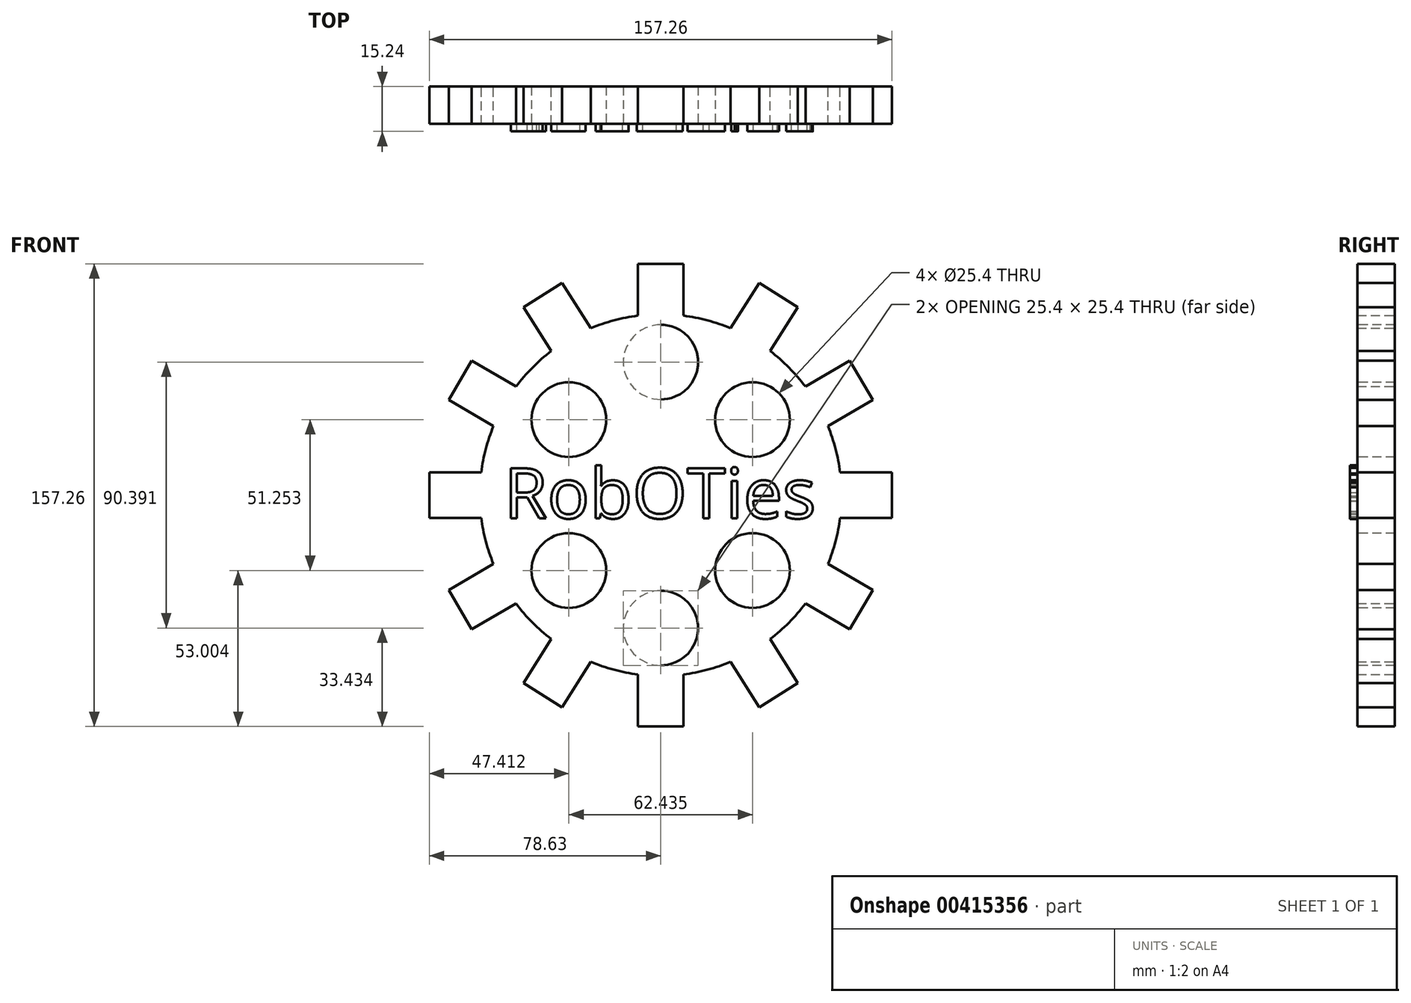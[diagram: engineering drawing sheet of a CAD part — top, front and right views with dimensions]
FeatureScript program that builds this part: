
annotation { "Feature Type Name" : "Feature", "Feature Type Description" : "" }
export const myFeature = defineFeature(function(context is Context, id is Id, definition is map)
    precondition{}
    {
        {
            var Q0;
            Q0=qCreatedBy(makeId("Front.planeOp"),FACE);
            var sketch = newSketch(context, id + "F0", { "sketchPlane" : qUnion([Q0])});
            skArc(sketch, "E0", {"start": v(-61, 7.73) * mm, "mid": v(-59.45, 15.72) * mm, "end": v(-56.85, 23.43) * mm});
            skLineSegment(sketch, "E1", {"start": v(-61, 7.73) * mm, "end": v(-78.63, 7.73) * mm});
            skLineSegment(sketch, "E2", {"start": v(-78.63, 7.73) * mm, "end": v(-78.63, 0) * mm});
            skPoint(sketch, "E3.orphan", {"position": v(-61.49, 0) * mm});
            skLineSegment(sketch, "E4", {"start": v(-56.85, 23.43) * mm, "end": v(-72.07, 32.3) * mm});
            skLineSegment(sketch, "E5", {"start": v(-72.07, 32.3) * mm, "end": v(-64.28, 45.66) * mm});
            skLineSegment(sketch, "E6", {"start": v(-64.28, 45.66) * mm, "end": v(-49.2, 36.87) * mm});
            skArc(sketch, "E7.trimOffspring", {"start": v(-49.2, 36.87) * mm, "mid": v(-43.62, 43.33) * mm, "end": v(-37.2, 48.96) * mm});
            skLineSegment(sketch, "E8", {"start": v(-37.2, 48.96) * mm, "end": v(-46.61, 63.86) * mm});
            skLineSegment(sketch, "E9", {"start": v(-46.61, 63.86) * mm, "end": v(-33.54, 72.13) * mm});
            skLineSegment(sketch, "E10", {"start": v(-33.54, 72.13) * mm, "end": v(-23.78, 56.7) * mm});
            skArc(sketch, "E11.trimOffspring", {"start": v(-23.78, 56.7) * mm, "mid": v(-15.91, 59.4) * mm, "end": v(-7.75, 61) * mm});
            skLineSegment(sketch, "E12", {"start": v(-7.75, 61) * mm, "end": v(-7.75, 78.63) * mm});
            skLineSegment(sketch, "E13", {"start": v(-7.75, 78.63) * mm, "end": v(0, 78.63) * mm});
            skPoint(sketch, "E14.orphan", {"position": v(0, 61.49) * mm});
            skLineSegment(sketch, "E15", {"start": v(0, -76.88) * mm, "end": v(0, 112.3) * mm, "construction": true});
            skLineSegment(sketch, "E16", {"start": v(103.9, 0) * mm, "end": v(-126.27, 0) * mm, "construction": true});
            skLineSegment(sketch, "E17.MirrorCS", {"start": v(7.75, 61) * mm, "end": v(7.75, 78.63) * mm});
            skLineSegment(sketch, "E18.MirrorCS", {"start": v(7.75, 78.63) * mm, "end": v(0, 78.63) * mm});
            skArc(sketch, "E19.MirrorCS", {"start": v(23.78, 56.7) * mm, "mid": v(15.91, 59.4) * mm, "end": v(7.75, 61) * mm});
            skLineSegment(sketch, "E20.MirrorCS", {"start": v(33.54, 72.13) * mm, "end": v(23.78, 56.7) * mm});
            skLineSegment(sketch, "E21.MirrorCS", {"start": v(46.61, 63.86) * mm, "end": v(33.54, 72.13) * mm});
            skLineSegment(sketch, "E22.MirrorCS", {"start": v(37.2, 48.96) * mm, "end": v(46.61, 63.86) * mm});
            skArc(sketch, "E23.MirrorCS", {"start": v(49.2, 36.87) * mm, "mid": v(43.62, 43.33) * mm, "end": v(37.2, 48.96) * mm});
            skLineSegment(sketch, "E24.MirrorCS", {"start": v(64.28, 45.66) * mm, "end": v(49.2, 36.87) * mm});
            skLineSegment(sketch, "E25.MirrorCS", {"start": v(72.07, 32.3) * mm, "end": v(64.28, 45.66) * mm});
            skLineSegment(sketch, "E26.MirrorCS", {"start": v(56.85, 23.43) * mm, "end": v(72.07, 32.3) * mm});
            skArc(sketch, "E27.MirrorCS", {"start": v(61, 7.73) * mm, "mid": v(59.45, 15.72) * mm, "end": v(56.85, 23.43) * mm});
            skLineSegment(sketch, "E28.MirrorCS", {"start": v(61, 7.73) * mm, "end": v(78.63, 7.73) * mm});
            skLineSegment(sketch, "E29.MirrorCS", {"start": v(78.63, 7.73) * mm, "end": v(78.63, 0) * mm});
            skLineSegment(sketch, "E30.MirrorCS", {"start": v(-78.63, -7.73) * mm, "end": v(-78.63, 0) * mm});
            skLineSegment(sketch, "E31.MirrorCS", {"start": v(-61, -7.73) * mm, "end": v(-78.63, -7.73) * mm});
            skArc(sketch, "E32.MirrorCS", {"start": v(-61, -7.73) * mm, "mid": v(-59.45, -15.72) * mm, "end": v(-56.85, -23.43) * mm});
            skLineSegment(sketch, "E33.MirrorCS", {"start": v(-56.85, -23.43) * mm, "end": v(-72.07, -32.3) * mm});
            skLineSegment(sketch, "E34.MirrorCS", {"start": v(-72.07, -32.3) * mm, "end": v(-64.28, -45.66) * mm});
            skLineSegment(sketch, "E35.MirrorCS", {"start": v(-64.28, -45.66) * mm, "end": v(-49.2, -36.87) * mm});
            skArc(sketch, "E36.MirrorCS", {"start": v(-49.2, -36.87) * mm, "mid": v(-43.62, -43.33) * mm, "end": v(-37.2, -48.96) * mm});
            skLineSegment(sketch, "E37.MirrorCS", {"start": v(-37.2, -48.96) * mm, "end": v(-46.61, -63.86) * mm});
            skLineSegment(sketch, "E38.MirrorCS", {"start": v(-46.61, -63.86) * mm, "end": v(-33.54, -72.13) * mm});
            skLineSegment(sketch, "E39.MirrorCS", {"start": v(-33.54, -72.13) * mm, "end": v(-23.78, -56.7) * mm});
            skArc(sketch, "E40.MirrorCS", {"start": v(-23.78, -56.7) * mm, "mid": v(-15.91, -59.4) * mm, "end": v(-7.75, -61) * mm});
            skLineSegment(sketch, "E41.MirrorCS", {"start": v(-7.75, -61) * mm, "end": v(-7.75, -78.63) * mm});
            skLineSegment(sketch, "E42.MirrorCS", {"start": v(-7.75, -78.63) * mm, "end": v(0, -78.63) * mm});
            skLineSegment(sketch, "E43.MirrorCS", {"start": v(7.75, -78.63) * mm, "end": v(0, -78.63) * mm});
            skLineSegment(sketch, "E44.MirrorCS", {"start": v(7.75, -61) * mm, "end": v(7.75, -78.63) * mm});
            skArc(sketch, "E45.MirrorCS", {"start": v(23.78, -56.7) * mm, "mid": v(15.91, -59.4) * mm, "end": v(7.75, -61) * mm});
            skLineSegment(sketch, "E46.MirrorCS", {"start": v(33.54, -72.13) * mm, "end": v(23.78, -56.7) * mm});
            skLineSegment(sketch, "E47.MirrorCS", {"start": v(46.61, -63.86) * mm, "end": v(33.54, -72.13) * mm});
            skLineSegment(sketch, "E48.MirrorCS", {"start": v(37.2, -48.96) * mm, "end": v(46.61, -63.86) * mm});
            skArc(sketch, "E49.MirrorCS", {"start": v(49.2, -36.87) * mm, "mid": v(43.62, -43.33) * mm, "end": v(37.2, -48.96) * mm});
            skLineSegment(sketch, "E50.MirrorCS", {"start": v(64.28, -45.66) * mm, "end": v(49.2, -36.87) * mm});
            skLineSegment(sketch, "E51.MirrorCS", {"start": v(72.07, -32.3) * mm, "end": v(64.28, -45.66) * mm});
            skLineSegment(sketch, "E52.MirrorCS", {"start": v(56.85, -23.43) * mm, "end": v(72.07, -32.3) * mm});
            skArc(sketch, "E53.MirrorCS", {"start": v(61, -7.73) * mm, "mid": v(59.45, -15.72) * mm, "end": v(56.85, -23.43) * mm});
            skLineSegment(sketch, "E54.MirrorCS", {"start": v(61, -7.73) * mm, "end": v(78.63, -7.73) * mm});
            skLineSegment(sketch, "E55.MirrorCS", {"start": v(78.63, -7.73) * mm, "end": v(78.63, 0) * mm});
            skSolve(sketch);
        }
        {
            var Q0;
            Q0 = qSketchRegion(id + "F0", true);
            extrude(context, id + "F1", {"entities" : qUnion([Q0]), "depth" : 12.7 * mm});
        }
        {
            var Q0;
            Q0=makeQuery(id+"F1.opExtrude","CAP_FACE",FACE,{"disambiguationData":[OSD([sQuery(id+"F0.wireOp",EDGE,"E0"),sQuery(id+"F0.wireOp",EDGE,"E1"),sQuery(id+"F0.wireOp",EDGE,"E2"),sQuery(id+"F0.wireOp",EDGE,"E4"),sQuery(id+"F0.wireOp",EDGE,"E5"),sQuery(id+"F0.wireOp",EDGE,"E6"),sQuery(id+"F0.wireOp",EDGE,"E7.trimOffspring"),sQuery(id+"F0.wireOp",EDGE,"E8"),sQuery(id+"F0.wireOp",EDGE,"E9"),sQuery(id+"F0.wireOp",EDGE,"E10"),sQuery(id+"F0.wireOp",EDGE,"E11.trimOffspring"),sQuery(id+"F0.wireOp",EDGE,"E12"),sQuery(id+"F0.wireOp",EDGE,"E13"),sQuery(id+"F0.wireOp",EDGE,"E17.MirrorCS"),sQuery(id+"F0.wireOp",EDGE,"E18.MirrorCS"),sQuery(id+"F0.wireOp",EDGE,"E19.MirrorCS"),sQuery(id+"F0.wireOp",EDGE,"E20.MirrorCS"),sQuery(id+"F0.wireOp",EDGE,"E21.MirrorCS"),sQuery(id+"F0.wireOp",EDGE,"E22.MirrorCS"),sQuery(id+"F0.wireOp",EDGE,"E23.MirrorCS"),sQuery(id+"F0.wireOp",EDGE,"E24.MirrorCS"),sQuery(id+"F0.wireOp",EDGE,"E25.MirrorCS"),sQuery(id+"F0.wireOp",EDGE,"E26.MirrorCS"),sQuery(id+"F0.wireOp",EDGE,"E27.MirrorCS"),sQuery(id+"F0.wireOp",EDGE,"E28.MirrorCS"),sQuery(id+"F0.wireOp",EDGE,"E29.MirrorCS"),sQuery(id+"F0.wireOp",EDGE,"E30.MirrorCS"),sQuery(id+"F0.wireOp",EDGE,"E31.MirrorCS"),sQuery(id+"F0.wireOp",EDGE,"E32.MirrorCS"),sQuery(id+"F0.wireOp",EDGE,"E33.MirrorCS"),sQuery(id+"F0.wireOp",EDGE,"E34.MirrorCS"),sQuery(id+"F0.wireOp",EDGE,"E35.MirrorCS"),sQuery(id+"F0.wireOp",EDGE,"E36.MirrorCS"),sQuery(id+"F0.wireOp",EDGE,"E37.MirrorCS"),sQuery(id+"F0.wireOp",EDGE,"E38.MirrorCS"),sQuery(id+"F0.wireOp",EDGE,"E39.MirrorCS"),sQuery(id+"F0.wireOp",EDGE,"E40.MirrorCS"),sQuery(id+"F0.wireOp",EDGE,"E41.MirrorCS"),sQuery(id+"F0.wireOp",EDGE,"E42.MirrorCS"),sQuery(id+"F0.wireOp",EDGE,"E43.MirrorCS"),sQuery(id+"F0.wireOp",EDGE,"E44.MirrorCS"),sQuery(id+"F0.wireOp",EDGE,"E45.MirrorCS"),sQuery(id+"F0.wireOp",EDGE,"E46.MirrorCS"),sQuery(id+"F0.wireOp",EDGE,"E47.MirrorCS"),sQuery(id+"F0.wireOp",EDGE,"E48.MirrorCS"),sQuery(id+"F0.wireOp",EDGE,"E49.MirrorCS"),sQuery(id+"F0.wireOp",EDGE,"E50.MirrorCS"),sQuery(id+"F0.wireOp",EDGE,"E51.MirrorCS"),sQuery(id+"F0.wireOp",EDGE,"E52.MirrorCS"),sQuery(id+"F0.wireOp",EDGE,"E53.MirrorCS"),sQuery(id+"F0.wireOp",EDGE,"E54.MirrorCS"),sQuery(id+"F0.wireOp",EDGE,"E55.MirrorCS")])],"isStart":false});
            var sketch = newSketch(context, id + "F2", { "sketchPlane" : qUnion([Q0])});
            skLineSegment(sketch, "E56", {"start": v(0, 111.36) * mm, "end": v(0, -102.5) * mm, "construction": true});
            skPoint(sketch, "E56.startSnap0", {"position": v(0, 78.63) * mm});
            skPoint(sketch, "E56.endSnap0", {"position": v(0, -78.63) * mm});
            skLineSegment(sketch, "E57", {"start": v(-109.03, 0) * mm, "end": v(117.88, 0) * mm, "construction": true});
            skCircle(sketch, "E58", {"center": v(-31.22, 25.63) * mm, "radius": 12.7 * mm});
            skArc(sketch, "E59", {"start": v(0, 57.9) * mm, "mid": v(-12.7, 45.2) * mm, "end": v(0, 32.5) * mm});
            skArc(sketch, "E60.MirrorCS", {"start": v(0, 57.9) * mm, "mid": v(12.7, 45.2) * mm, "end": v(0, 32.5) * mm});
            skCircle(sketch, "E61.MirrorC", {"center": v(31.22, 25.63) * mm, "radius": 12.7 * mm});
            skCircle(sketch, "E62.MirrorC", {"center": v(-31.22, -25.63) * mm, "radius": 12.7 * mm});
            skArc(sketch, "E63.MirrorCS", {"start": v(0, -57.9) * mm, "mid": v(-12.7, -45.2) * mm, "end": v(0, -32.5) * mm});
            skArc(sketch, "E64.MirrorCS", {"start": v(0, -57.9) * mm, "mid": v(12.7, -45.2) * mm, "end": v(0, -32.5) * mm});
            skCircle(sketch, "E65.MirrorC", {"center": v(31.22, -25.63) * mm, "radius": 12.7 * mm});
            skSolve(sketch);
        }
        {
            var Q0;
            Q0 = qSketchRegion(id + "F2", true);
            extrude(context, id + "F3", {"entities" : qUnion([Q0]), "operationType" : NewBodyOperationType.REMOVE, "oppositeDirection" : true, "depth" : 25.4 * mm});
        }
        {
            var Q0;
            Q0=makeQuery(id+"F1.opExtrude","CAP_FACE",FACE,{"disambiguationData":[OSD([sQuery(id+"F0.wireOp",EDGE,"E0"),sQuery(id+"F0.wireOp",EDGE,"E1"),sQuery(id+"F0.wireOp",EDGE,"E2"),sQuery(id+"F0.wireOp",EDGE,"E4"),sQuery(id+"F0.wireOp",EDGE,"E5"),sQuery(id+"F0.wireOp",EDGE,"E6"),sQuery(id+"F0.wireOp",EDGE,"E7.trimOffspring"),sQuery(id+"F0.wireOp",EDGE,"E8"),sQuery(id+"F0.wireOp",EDGE,"E9"),sQuery(id+"F0.wireOp",EDGE,"E10"),sQuery(id+"F0.wireOp",EDGE,"E11.trimOffspring"),sQuery(id+"F0.wireOp",EDGE,"E12"),sQuery(id+"F0.wireOp",EDGE,"E13"),sQuery(id+"F0.wireOp",EDGE,"E17.MirrorCS"),sQuery(id+"F0.wireOp",EDGE,"E18.MirrorCS"),sQuery(id+"F0.wireOp",EDGE,"E19.MirrorCS"),sQuery(id+"F0.wireOp",EDGE,"E20.MirrorCS"),sQuery(id+"F0.wireOp",EDGE,"E21.MirrorCS"),sQuery(id+"F0.wireOp",EDGE,"E22.MirrorCS"),sQuery(id+"F0.wireOp",EDGE,"E23.MirrorCS"),sQuery(id+"F0.wireOp",EDGE,"E24.MirrorCS"),sQuery(id+"F0.wireOp",EDGE,"E25.MirrorCS"),sQuery(id+"F0.wireOp",EDGE,"E26.MirrorCS"),sQuery(id+"F0.wireOp",EDGE,"E27.MirrorCS"),sQuery(id+"F0.wireOp",EDGE,"E28.MirrorCS"),sQuery(id+"F0.wireOp",EDGE,"E29.MirrorCS"),sQuery(id+"F0.wireOp",EDGE,"E30.MirrorCS"),sQuery(id+"F0.wireOp",EDGE,"E31.MirrorCS"),sQuery(id+"F0.wireOp",EDGE,"E32.MirrorCS"),sQuery(id+"F0.wireOp",EDGE,"E33.MirrorCS"),sQuery(id+"F0.wireOp",EDGE,"E34.MirrorCS"),sQuery(id+"F0.wireOp",EDGE,"E35.MirrorCS"),sQuery(id+"F0.wireOp",EDGE,"E36.MirrorCS"),sQuery(id+"F0.wireOp",EDGE,"E37.MirrorCS"),sQuery(id+"F0.wireOp",EDGE,"E38.MirrorCS"),sQuery(id+"F0.wireOp",EDGE,"E39.MirrorCS"),sQuery(id+"F0.wireOp",EDGE,"E40.MirrorCS"),sQuery(id+"F0.wireOp",EDGE,"E41.MirrorCS"),sQuery(id+"F0.wireOp",EDGE,"E42.MirrorCS"),sQuery(id+"F0.wireOp",EDGE,"E43.MirrorCS"),sQuery(id+"F0.wireOp",EDGE,"E44.MirrorCS"),sQuery(id+"F0.wireOp",EDGE,"E45.MirrorCS"),sQuery(id+"F0.wireOp",EDGE,"E46.MirrorCS"),sQuery(id+"F0.wireOp",EDGE,"E47.MirrorCS"),sQuery(id+"F0.wireOp",EDGE,"E48.MirrorCS"),sQuery(id+"F0.wireOp",EDGE,"E49.MirrorCS"),sQuery(id+"F0.wireOp",EDGE,"E50.MirrorCS"),sQuery(id+"F0.wireOp",EDGE,"E51.MirrorCS"),sQuery(id+"F0.wireOp",EDGE,"E52.MirrorCS"),sQuery(id+"F0.wireOp",EDGE,"E53.MirrorCS"),sQuery(id+"F0.wireOp",EDGE,"E54.MirrorCS"),sQuery(id+"F0.wireOp",EDGE,"E55.MirrorCS")])],"isStart":false});
            var sketch = newSketch(context, id + "F4", { "sketchPlane" : qUnion([Q0])});
            skText(sketch, "E66", { "text": "RobOTies", "fontName": "OpenSans-Regular.ttf"});
            const initialGuessF4  = {"E66": [-0.05323, -0.0079, 1, 0, 0.01712]};
            skSetInitialGuess(sketch, initialGuessF4);
            skSolve(sketch);
        }
        {
            var Q0;
            Q0 = qSketchRegion(id + "F4", true);
            extrude(context, id + "F5", {"entities" : qUnion([Q0]), "operationType" : NewBodyOperationType.ADD, "depth" : 2.54 * mm});
        }
    });
